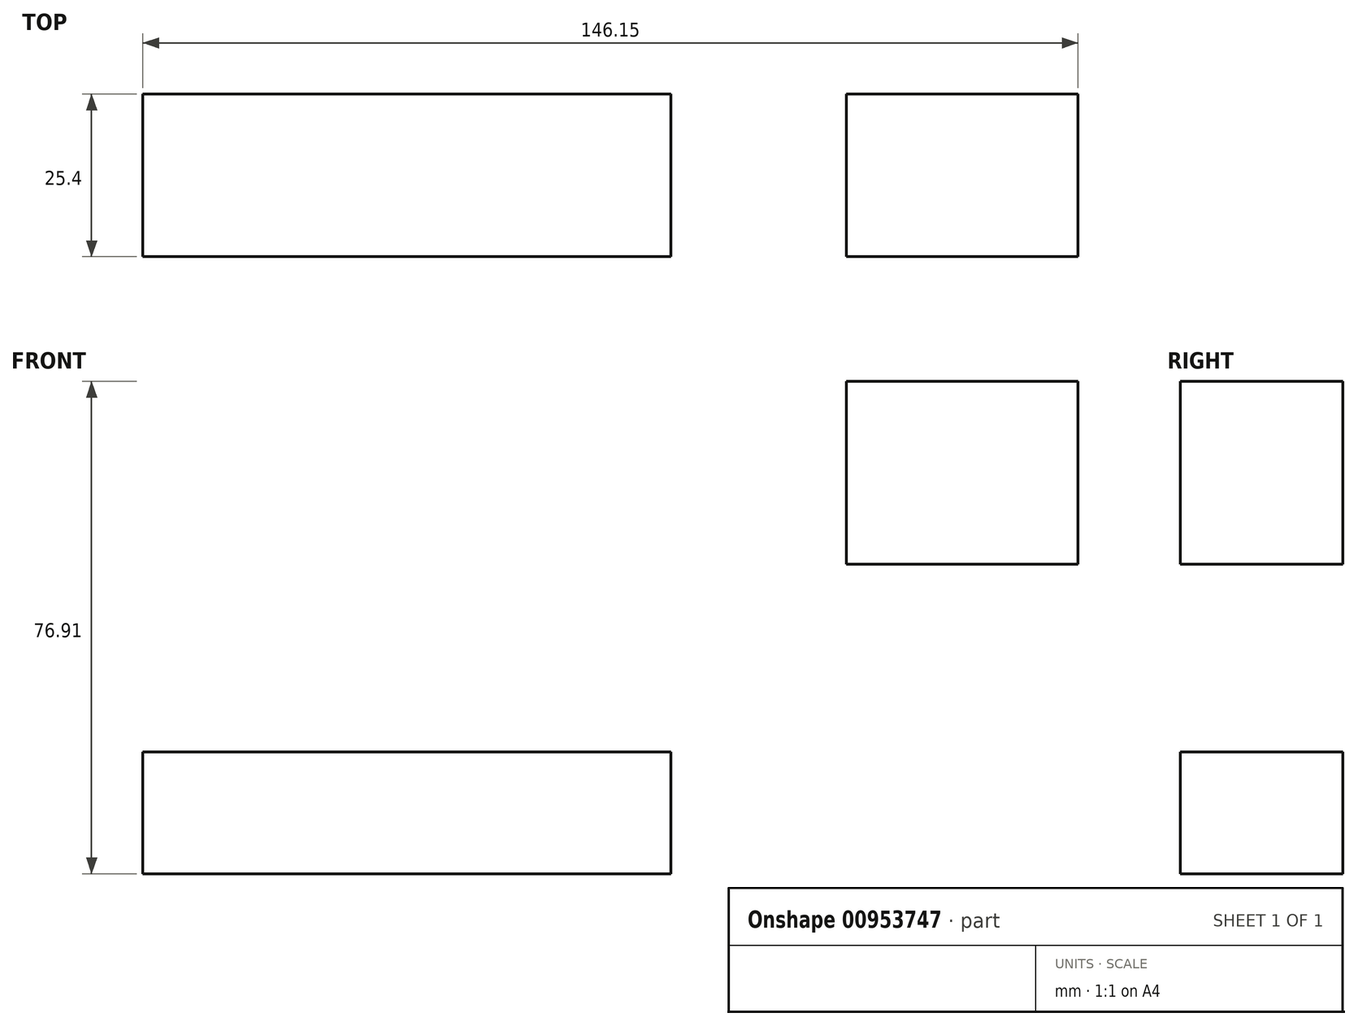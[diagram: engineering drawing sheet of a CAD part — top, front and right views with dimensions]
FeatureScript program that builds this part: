
annotation { "Feature Type Name" : "Feature", "Feature Type Description" : "" }
export const myFeature = defineFeature(function(context is Context, id is Id, definition is map)
    precondition{}
    {
        {
            var Q0;
            Q0=qCreatedBy(makeId("Front.planeOp"),FACE);
            var sketch = newSketch(context, id + "F0", { "sketchPlane" : qUnion([Q0])});
            skLineSegment(sketch, "E0.bottom", {"start": v(41.27, 9.53) * mm, "end": v(-41.28, 9.53) * mm});
            skLineSegment(sketch, "E0.top", {"start": v(41.28, -9.52) * mm, "end": v(-41.27, -9.52) * mm});
            skLineSegment(sketch, "E0.left", {"start": v(41.28, 9.53) * mm, "end": v(41.28, -9.52) * mm});
            skLineSegment(sketch, "E0.right", {"start": v(-41.28, 9.53) * mm, "end": v(-41.28, -9.52) * mm});
            skPoint(sketch, "E0.middle", {"position": v(0, 0) * mm});
            skLineSegment(sketch, "E1.bottom", {"start": v(68.7, 67.38) * mm, "end": v(104.88, 67.38) * mm});
            skLineSegment(sketch, "E1.top", {"start": v(68.7, 38.8) * mm, "end": v(104.88, 38.8) * mm});
            skLineSegment(sketch, "E1.left", {"start": v(68.7, 67.38) * mm, "end": v(68.7, 38.8) * mm});
            skLineSegment(sketch, "E1.right", {"start": v(104.88, 67.38) * mm, "end": v(104.88, 38.8) * mm});
            skPoint(sketch, "E1.middle", {"position": v(86.8, 53.09) * mm});
            skLineSegment(sketch, "E2", {"start": v(41.27, 9.53) * mm, "end": v(41.27, 16.6) * mm});
            skArc(sketch, "E3", {"start": v(41.27, 16.6) * mm, "mid": v(48.97, 35.18) * mm, "end": v(67.55, 42.88) * mm});
            skLineSegment(sketch, "E4", {"start": v(67.55, 42.88) * mm, "end": v(86.8, 42.88) * mm});
            skSolve(sketch);
        }
        {
            var Q0;
            Q0 = qSketchRegion(id + "F0", true);
            extrude(context, id + "F1", {"entities" : qUnion([Q0]), "depth" : 25.4 * mm, "offsetDistance" : 25.4 * mm});
        }
    });
